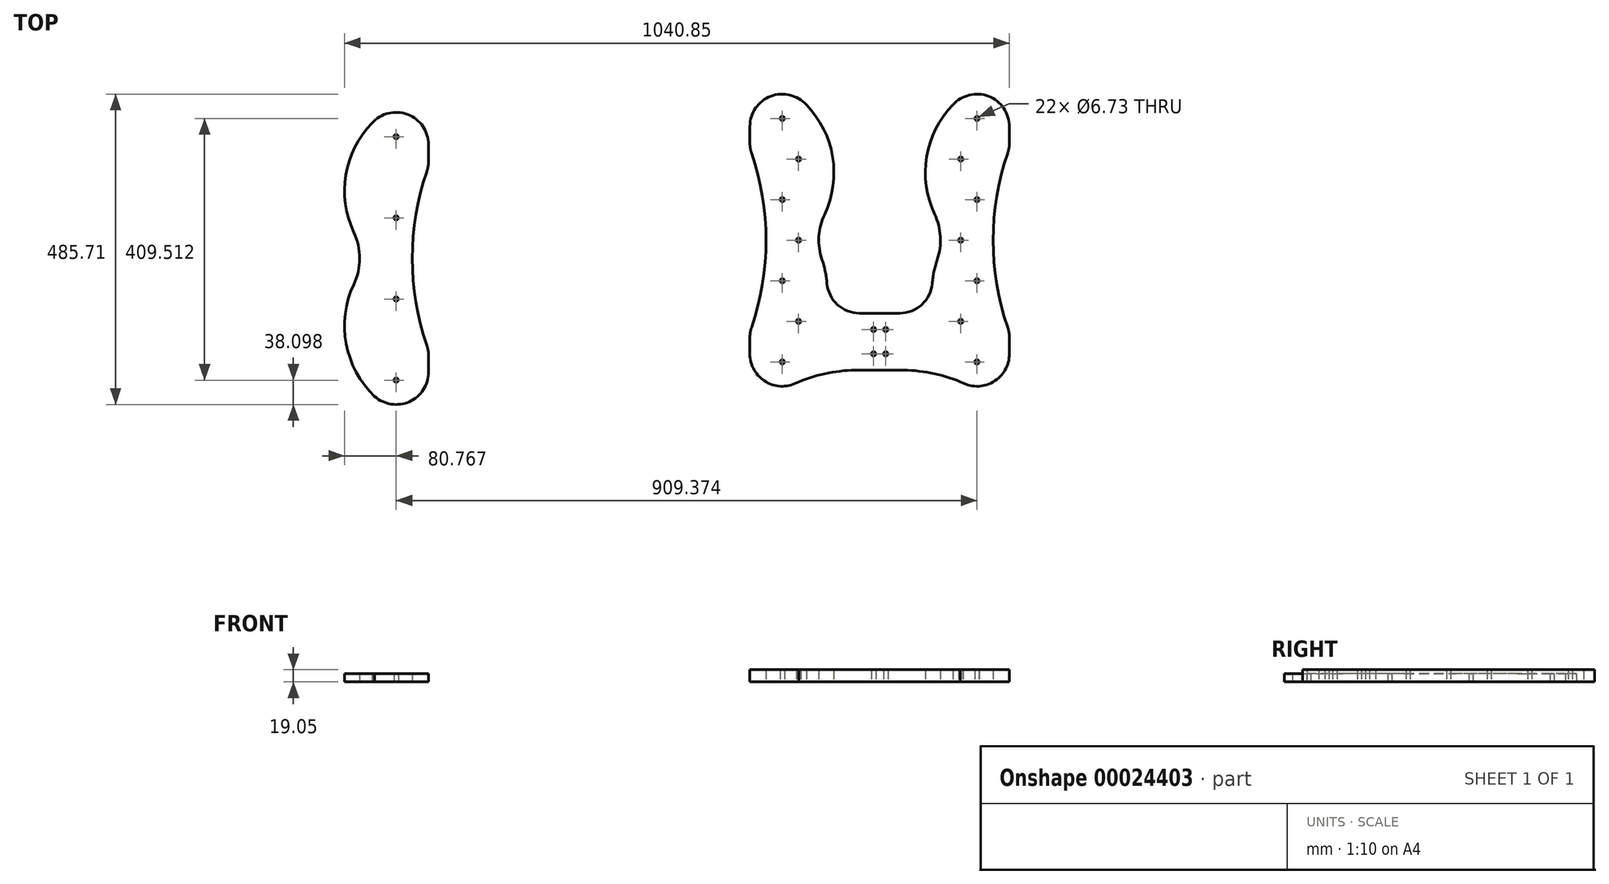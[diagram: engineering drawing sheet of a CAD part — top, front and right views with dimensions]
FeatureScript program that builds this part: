
annotation { "Feature Type Name" : "Feature", "Feature Type Description" : "" }
export const myFeature = defineFeature(function(context is Context, id is Id, definition is map)
    precondition{}
    {
        {
            var Q0;
            Q0=qCreatedBy(makeId("Top.planeOp"),FACE);
            var sketch = newSketch(context, id + "F0", { "sketchPlane" : qUnion([Q0])});
            skLineSegment(sketch, "E0.bottom", {"start": v(0, 0) * mm, "end": v(50.8, 0) * mm, "construction": true});
            skLineSegment(sketch, "E0.top", {"start": v(0, 457.2) * mm, "end": v(50.8, 457.2) * mm, "construction": true});
            skLineSegment(sketch, "E0.left", {"start": v(0, 0) * mm, "end": v(0, 50.8) * mm, "construction": true});
            skLineSegment(sketch, "E0.right", {"start": v(406.3, 0) * mm, "end": v(406.3, 50.8) * mm, "construction": true});
            skArc(sketch, "E1", {"start": v(0, 50.8) * mm, "mid": v(14.88, 14.88) * mm, "end": v(50.8, 0) * mm});
            skArc(sketch, "E2", {"start": v(355.5, 0) * mm, "mid": v(391.42, 14.88) * mm, "end": v(406.3, 50.8) * mm});
            skArc(sketch, "E3", {"start": v(50.8, 457.2) * mm, "mid": v(14.88, 442.32) * mm, "end": v(0, 406.4) * mm});
            skLineSegment(sketch, "E4", {"start": v(0, 50.8) * mm, "end": v(0, 76.2) * mm});
            skLineSegment(sketch, "E5", {"start": v(50.8, 0) * mm, "end": v(203.15, 0) * mm, "construction": true});
            skLineSegment(sketch, "E6", {"start": v(355.5, 0) * mm, "end": v(406.3, 0) * mm, "construction": true});
            skLineSegment(sketch, "E7", {"start": v(0, 406.4) * mm, "end": v(0, 457.2) * mm, "construction": true});
            skArc(sketch, "E8", {"start": v(406.3, 406.4) * mm, "mid": v(391.42, 442.32) * mm, "end": v(355.5, 457.2) * mm});
            skLineSegment(sketch, "E9", {"start": v(406.3, 50.8) * mm, "end": v(406.3, 76.2) * mm});
            skLineSegment(sketch, "E10", {"start": v(50.8, 457.2) * mm, "end": v(355.6, 457.2) * mm, "construction": true});
            skLineSegment(sketch, "E11", {"start": v(355.6, 457.2) * mm, "end": v(406.3, 457.2) * mm, "construction": true});
            skLineSegment(sketch, "E12", {"start": v(406.3, 406.4) * mm, "end": v(406.3, 457.2) * mm, "construction": true});
            skArc(sketch, "E13", {"start": v(117, 269.24) * mm, "mid": v(129, 362.1) * mm, "end": v(84.44, 444.46) * mm});
            skArc(sketch, "E14", {"start": v(120.77, 160.88) * mm, "mid": v(137, 127.72) * mm, "end": v(171.4, 114.3) * mm});
            skArc(sketch, "E15", {"start": v(234.9, 114.3) * mm, "mid": v(269.3, 127.72) * mm, "end": v(285.52, 160.88) * mm});
            skLineSegment(sketch, "E16", {"start": v(203.15, 0) * mm, "end": v(355.5, 0) * mm, "construction": true});
            skLineSegment(sketch, "E17", {"start": v(171.4, 114.3) * mm, "end": v(234.9, 114.3) * mm});
            skArc(sketch, "E18", {"start": v(293.24, 197.7) * mm, "mid": v(298.25, 233.85) * mm, "end": v(289.3, 269.24) * mm});
            skLineSegment(sketch, "E19", {"start": v(203.15, 0) * mm, "end": v(203.15, 457.2) * mm, "construction": true});
            skArc(sketch, "E20", {"start": v(321.86, 444.47) * mm, "mid": v(277.3, 362.1) * mm, "end": v(289.3, 269.24) * mm});
            skArc(sketch, "E21.trimOffspring", {"start": v(117, 269.24) * mm, "mid": v(108.04, 233.85) * mm, "end": v(113.05, 197.7) * mm});
            skArc(sketch, "E22", {"start": v(4.27, 0) * mm, "mid": v(15.01, 2.98) * mm, "end": v(25.5, 6.74) * mm});
            skArc(sketch, "E23", {"start": v(293.24, 197.7) * mm, "mid": v(288.24, 179.53) * mm, "end": v(285.52, 160.88) * mm});
            skArc(sketch, "E24.trimOffspring", {"start": v(120.77, 160.88) * mm, "mid": v(118.05, 179.53) * mm, "end": v(113.05, 197.7) * mm});
            skArc(sketch, "E25.trimOffspring", {"start": v(380.79, 6.74) * mm, "mid": v(391.29, 2.98) * mm, "end": v(402.03, 0) * mm});
            skArc(sketch, "E26", {"start": v(88.63, 440.3) * mm, "mid": v(32.65, 453.85) * mm, "end": v(0, 406.4) * mm});
            skArc(sketch, "E27", {"start": v(406.3, 406.3) * mm, "mid": v(373.7, 453.83) * mm, "end": v(317.67, 440.3) * mm});
            skLineSegment(sketch, "E28", {"start": v(0, 228.6) * mm, "end": v(25.4, 228.6) * mm, "construction": true});
            skLineSegment(sketch, "E29", {"start": v(406.3, 228.6) * mm, "end": v(380.9, 228.6) * mm, "construction": true});
            skArc(sketch, "E30", {"start": v(403.55, 364.52) * mm, "mid": v(380.9, 228.6) * mm, "end": v(403.55, 92.68) * mm});
            skLineSegment(sketch, "E31", {"start": v(406.3, 228.6) * mm, "end": v(800, 228.6) * mm, "construction": true});
            skLineSegment(sketch, "E32", {"start": v(0, 228.6) * mm, "end": v(-393.7, 228.6) * mm, "construction": true});
            skLineSegment(sketch, "E33", {"start": v(-933.81, 228.6) * mm, "end": v(-1296.84, 228.6) * mm, "construction": true});
            skArc(sketch, "E34", {"start": v(2.75, 92.68) * mm, "mid": v(25.4, 228.6) * mm, "end": v(2.75, 364.52) * mm});
            skLineSegment(sketch, "E35.trimOffspring", {"start": v(0, 381) * mm, "end": v(0, 406.4) * mm});
            skLineSegment(sketch, "E36.trimOffspring", {"start": v(406.3, 381) * mm, "end": v(406.3, 406.4) * mm});
            skArc(sketch, "E37", {"start": v(403.55, 364.52) * mm, "mid": v(405.6, 372.65) * mm, "end": v(406.3, 381) * mm});
            skArc(sketch, "E38", {"start": v(406.3, 76.2) * mm, "mid": v(405.6, 84.55) * mm, "end": v(403.55, 92.68) * mm});
            skArc(sketch, "E39", {"start": v(2.75, 92.68) * mm, "mid": v(0.7, 84.55) * mm, "end": v(0, 76.2) * mm});
            skArc(sketch, "E40", {"start": v(0, 381) * mm, "mid": v(0.7, 372.65) * mm, "end": v(2.75, 364.52) * mm});
            skArc(sketch, "E41", {"start": v(171.4, 25.4) * mm, "mid": v(123.14, 20.77) * mm, "end": v(76.64, 7.06) * mm});
            skLineSegment(sketch, "E42", {"start": v(171.4, 114.3) * mm, "end": v(171.4, -228.6) * mm, "construction": true});
            skLineSegment(sketch, "E43", {"start": v(234.9, 114.3) * mm, "end": v(234.9, -228.6) * mm, "construction": true});
            skLineSegment(sketch, "E44", {"start": v(171.4, -228.6) * mm, "end": v(234.9, -228.6) * mm, "construction": true});
            skLineSegment(sketch, "E45", {"start": v(234.9, 25.4) * mm, "end": v(171.4, 25.4) * mm});
            skLineSegment(sketch, "E46", {"start": v(203.15, 0) * mm, "end": v(203.15, 25.4) * mm, "construction": true});
            skArc(sketch, "E47.trimOffspring", {"start": v(329.66, 7.06) * mm, "mid": v(283.16, 20.77) * mm, "end": v(234.9, 25.4) * mm});
            skArc(sketch, "E48", {"start": v(0, 50.8) * mm, "mid": v(25.62, 6.68) * mm, "end": v(76.64, 7.06) * mm});
            skArc(sketch, "E49", {"start": v(329.66, 7.06) * mm, "mid": v(380.68, 6.68) * mm, "end": v(406.3, 50.8) * mm});
            skLineSegment(sketch, "E50", {"start": v(50.8, 457.2) * mm, "end": v(50.8, 0) * mm, "construction": true});
            skLineSegment(sketch, "E51", {"start": v(355.6, 457.2) * mm, "end": v(355.5, 0) * mm, "construction": true});
            skLineSegment(sketch, "E52", {"start": v(330.2, 442.25) * mm, "end": v(330.1, 21.4) * mm, "construction": true});
            skLineSegment(sketch, "E53", {"start": v(76.2, 435.99) * mm, "end": v(76.2, 35.35) * mm, "construction": true});
            skCircle(sketch, "E54", {"center": v(355.5, 38.1) * mm, "radius": 3.37 * mm});
            skCircle(sketch, "E55", {"center": v(355.53, 165.1) * mm, "radius": 3.37 * mm});
            skCircle(sketch, "E56", {"center": v(355.56, 292.1) * mm, "radius": 3.37 * mm});
            skCircle(sketch, "E57", {"center": v(355.6, 419.1) * mm, "radius": 3.37 * mm});
            skCircle(sketch, "E58", {"center": v(50.8, 419.1) * mm, "radius": 3.37 * mm});
            skCircle(sketch, "E59", {"center": v(50.8, 292.1) * mm, "radius": 3.37 * mm});
            skCircle(sketch, "E60", {"center": v(50.8, 165.1) * mm, "radius": 3.37 * mm});
            skCircle(sketch, "E61", {"center": v(50.8, 38.1) * mm, "radius": 3.37 * mm});
            skCircle(sketch, "E62", {"center": v(76.2, 101.6) * mm, "radius": 3.37 * mm});
            skCircle(sketch, "E63", {"center": v(76.2, 228.6) * mm, "radius": 3.37 * mm});
            skCircle(sketch, "E64", {"center": v(76.2, 355.6) * mm, "radius": 3.37 * mm});
            skCircle(sketch, "E65", {"center": v(330.18, 355.6) * mm, "radius": 3.37 * mm});
            skCircle(sketch, "E66", {"center": v(330.15, 228.6) * mm, "radius": 3.37 * mm});
            skCircle(sketch, "E67", {"center": v(330.12, 101.6) * mm, "radius": 3.37 * mm});
            skCircle(sketch, "E68", {"center": v(193.62, 88.9) * mm, "radius": 3.37 * mm});
            skCircle(sketch, "E69", {"center": v(193.62, 50.8) * mm, "radius": 3.37 * mm});
            skCircle(sketch, "E70", {"center": v(212.67, 50.8) * mm, "radius": 3.37 * mm});
            skCircle(sketch, "E71", {"center": v(212.67, 88.9) * mm, "radius": 3.37 * mm});
            skSolve(sketch);
        }
        {
            var Q0;
            Q0 = qSketchRegion(id + "F0", true);
            extrude(context, id + "F1", {"entities" : qUnion([Q0]), "depth" : 19.05 * mm});
        }
        {
            var Q0;
            Q0=qCreatedBy(makeId("Top.planeOp"),FACE);
            var sketch = newSketch(context, id + "F2", { "sketchPlane" : qUnion([Q0])});
            skLineSegment(sketch, "E72.right", {"start": v(-502.98, -28.51) * mm, "end": v(-502.98, 22.29) * mm, "construction": true});
            skArc(sketch, "E73", {"start": v(-553.78, -28.51) * mm, "mid": v(-517.86, -13.63) * mm, "end": v(-502.98, 22.29) * mm});
            skLineSegment(sketch, "E74", {"start": v(-553.78, -28.51) * mm, "end": v(-502.98, -28.51) * mm, "construction": true});
            skArc(sketch, "E75", {"start": v(-502.98, 377.89) * mm, "mid": v(-517.86, 413.8) * mm, "end": v(-553.78, 428.69) * mm});
            skLineSegment(sketch, "E76", {"start": v(-502.98, 22.29) * mm, "end": v(-502.98, 47.69) * mm});
            skLineSegment(sketch, "E77", {"start": v(-858.58, 428.69) * mm, "end": v(-553.78, 428.69) * mm, "construction": true});
            skLineSegment(sketch, "E78", {"start": v(-553.78, 428.69) * mm, "end": v(-502.98, 428.69) * mm, "construction": true});
            skLineSegment(sketch, "E79", {"start": v(-502.98, 377.89) * mm, "end": v(-502.98, 428.69) * mm, "construction": true});
            skLineSegment(sketch, "E80", {"start": v(-706.13, -28.51) * mm, "end": v(-553.78, -28.51) * mm, "construction": true});
            skArc(sketch, "E81", {"start": v(-619.99, 159.45) * mm, "mid": v(-610.88, 200.09) * mm, "end": v(-619.99, 240.73) * mm});
            skArc(sketch, "E82", {"start": v(-587.42, 415.95) * mm, "mid": v(-631.99, 333.6) * mm, "end": v(-619.99, 240.73) * mm});
            skArc(sketch, "E83.trimOffspring", {"start": v(-528.5, -21.77) * mm, "mid": v(-518, -25.53) * mm, "end": v(-507.25, -28.51) * mm});
            skArc(sketch, "E84", {"start": v(-502.98, 377.89) * mm, "mid": v(-535.63, 425.33) * mm, "end": v(-591.6, 411.8) * mm});
            skLineSegment(sketch, "E85", {"start": v(-502.98, 200.09) * mm, "end": v(-528.38, 200.09) * mm, "construction": true});
            skArc(sketch, "E86", {"start": v(-505.73, 336.01) * mm, "mid": v(-528.38, 200.09) * mm, "end": v(-505.73, 64.16) * mm});
            skLineSegment(sketch, "E87", {"start": v(-502.98, 200.09) * mm, "end": v(-109.28, 200.09) * mm, "construction": true});
            skLineSegment(sketch, "E88.trimOffspring", {"start": v(-502.98, 352.49) * mm, "end": v(-502.98, 377.89) * mm});
            skArc(sketch, "E89", {"start": v(-505.73, 336.01) * mm, "mid": v(-503.67, 344.14) * mm, "end": v(-502.98, 352.49) * mm});
            skArc(sketch, "E90", {"start": v(-502.98, 47.69) * mm, "mid": v(-503.67, 56.04) * mm, "end": v(-505.73, 64.16) * mm});
            skLineSegment(sketch, "E91", {"start": v(-737.88, -257.11) * mm, "end": v(-674.38, -257.11) * mm, "construction": true});
            skArc(sketch, "E92", {"start": v(-587.42, -15.78) * mm, "mid": v(-532.9, -24.02) * mm, "end": v(-502.98, 22.29) * mm});
            skLineSegment(sketch, "E93", {"start": v(-553.78, 428.69) * mm, "end": v(-553.78, -28.51) * mm, "construction": true});
            skCircle(sketch, "E94", {"center": v(-553.78, 9.59) * mm, "radius": 3.37 * mm});
            skCircle(sketch, "E95", {"center": v(-553.78, 136.59) * mm, "radius": 3.37 * mm});
            skCircle(sketch, "E96", {"center": v(-553.78, 263.59) * mm, "radius": 3.37 * mm});
            skCircle(sketch, "E97", {"center": v(-553.78, 390.59) * mm, "radius": 3.37 * mm});
            skLineSegment(sketch, "E98", {"start": v(-482.15, 305.75) * mm, "end": v(-482.15, 94.42) * mm, "construction": true});
            skArc(sketch, "E99.trimOffspring", {"start": v(-619.99, 159.45) * mm, "mid": v(-631.99, 66.58) * mm, "end": v(-587.42, -15.78) * mm});
            skSolve(sketch);
        }
        {
            var Q0;
            Q0 = qSketchRegion(id + "F2", true);
            extrude(context, id + "F3", {"entities" : qUnion([Q0]), "depth" : 12.7 * mm});
        }
    });
